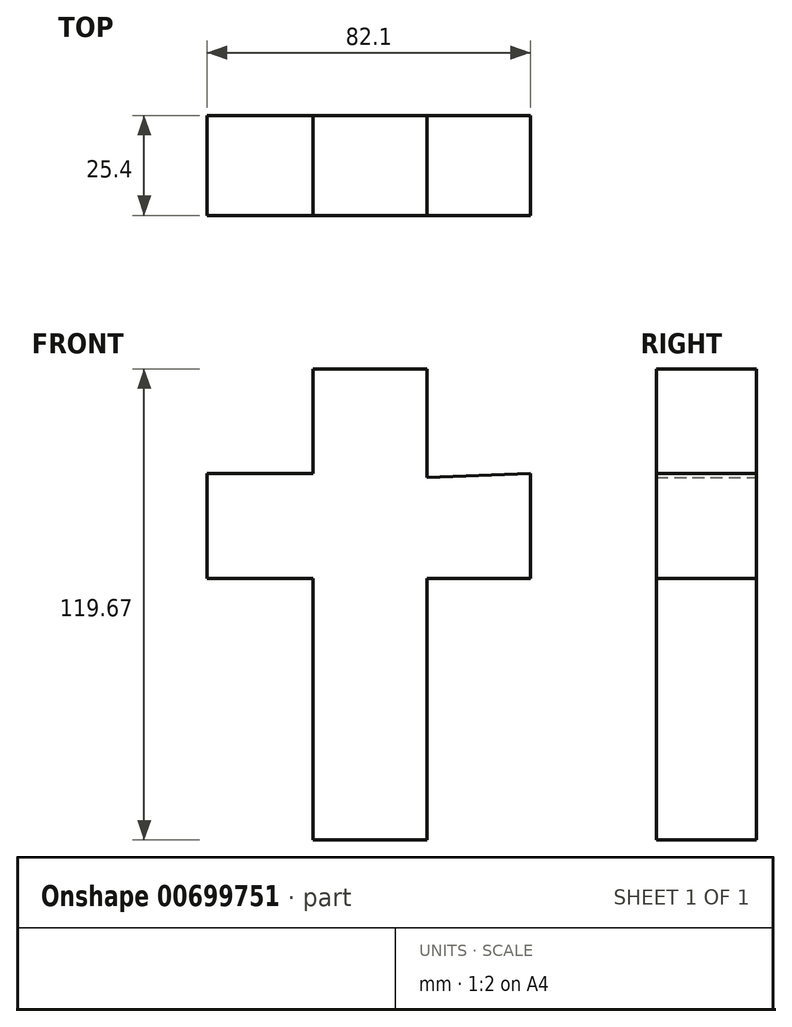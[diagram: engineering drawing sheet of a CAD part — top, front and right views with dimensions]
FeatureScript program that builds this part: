
annotation { "Feature Type Name" : "Feature", "Feature Type Description" : "" }
export const myFeature = defineFeature(function(context is Context, id is Id, definition is map)
    precondition{}
    {
        {
            var Q0;
            Q0=qCreatedBy(makeId("Front.planeOp"),FACE);
            var sketch = newSketch(context, id + "F0", { "sketchPlane" : qUnion([Q0])});
            skLineSegment(sketch, "E0", {"start": v(-5.21, 73.47) * mm, "end": v(-5.21, 46.87) * mm});
            skLineSegment(sketch, "E1", {"start": v(-31.47, 46.87) * mm, "end": v(-31.47, -19.6) * mm});
            skLineSegment(sketch, "E2", {"start": v(-31.47, -19.6) * mm, "end": v(-60.4, -19.6) * mm});
            skLineSegment(sketch, "E3", {"start": v(-60.4, -19.6) * mm, "end": v(-60.4, 46.87) * mm});
            skLineSegment(sketch, "E4", {"start": v(-60.4, 46.87) * mm, "end": v(-87.31, 46.87) * mm});
            skLineSegment(sketch, "E5", {"start": v(-87.31, 46.87) * mm, "end": v(-87.31, 73.47) * mm});
            skLineSegment(sketch, "E6", {"start": v(-87.31, 73.47) * mm, "end": v(-60.4, 73.47) * mm});
            skLineSegment(sketch, "E7", {"start": v(-60.4, 73.47) * mm, "end": v(-60.4, 100.06) * mm});
            skLineSegment(sketch, "E8", {"start": v(-60.4, 100.06) * mm, "end": v(-31.47, 100.06) * mm});
            skLineSegment(sketch, "E9", {"start": v(-31.47, 100.06) * mm, "end": v(-31.47, 72.47) * mm});
            skLineSegment(sketch, "E10", {"start": v(-31.47, 72.47) * mm, "end": v(-5.21, 73.47) * mm});
            skLineSegment(sketch, "E11", {"start": v(-5.21, 46.87) * mm, "end": v(-31.47, 46.87) * mm});
            skSolve(sketch);
        }
        {
            var Q0;
            Q0 = qSketchRegion(id + "F0", true);
            extrude(context, id + "F1", {"entities" : qUnion([Q0]), "depth" : 25.4 * mm, "offsetDistance" : 25.4 * mm});
        }
    });
